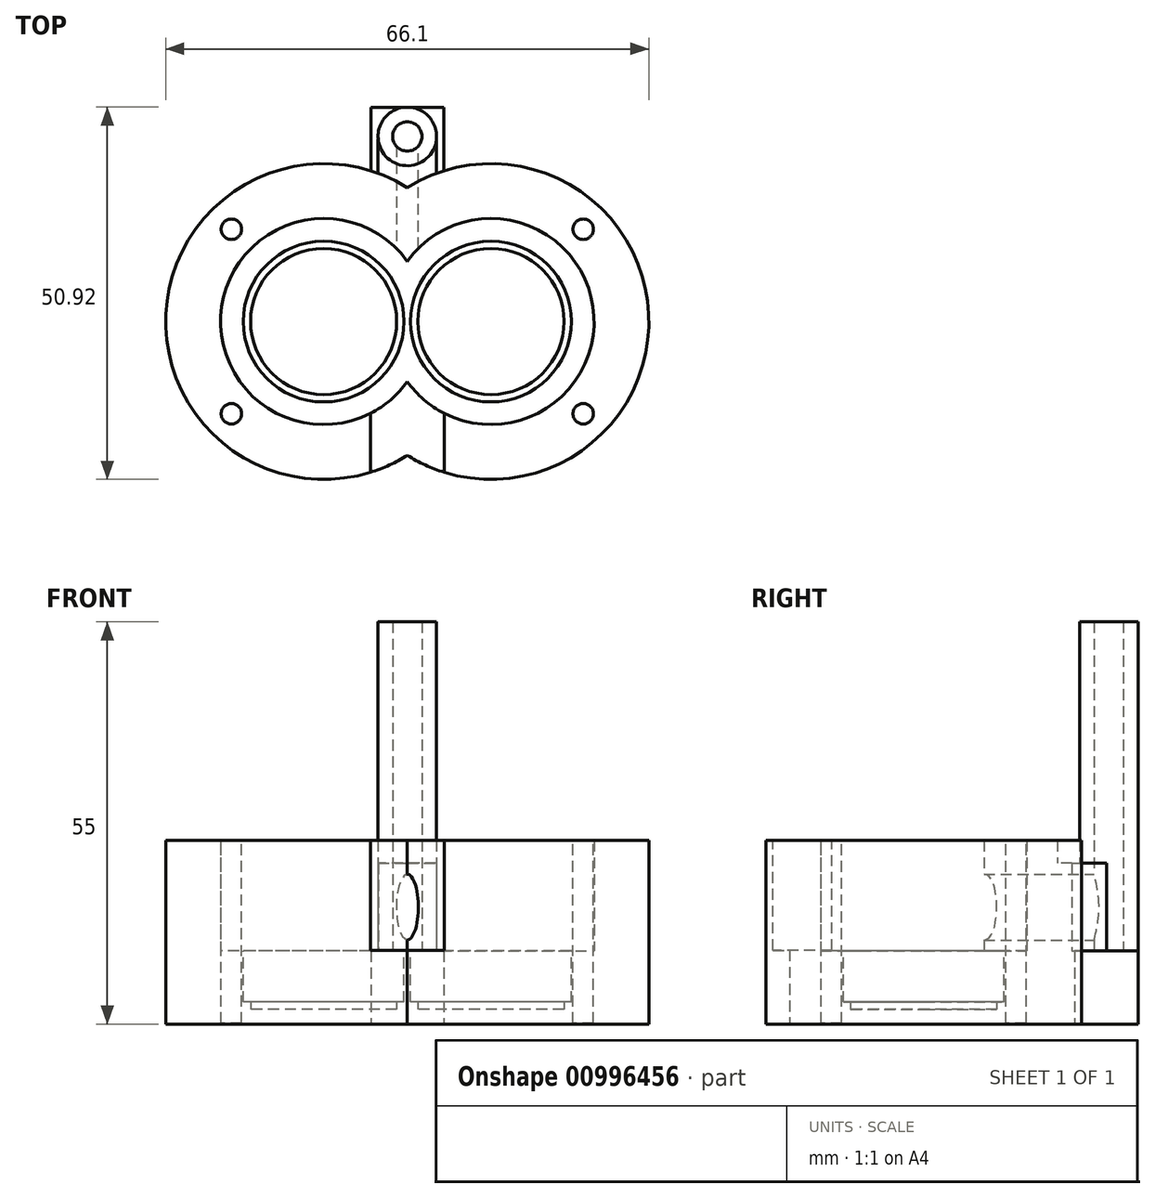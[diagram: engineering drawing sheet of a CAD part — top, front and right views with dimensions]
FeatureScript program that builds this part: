
annotation { "Feature Type Name" : "Feature", "Feature Type Description" : "" }
export const myFeature = defineFeature(function(context is Context, id is Id, definition is map)
    precondition{}
    {
        {
            var Q0;
            Q0=qCreatedBy(makeId("Top.planeOp"),FACE);
            var sketch = newSketch(context, id + "F0", { "sketchPlane" : qUnion([Q0])});
            skArc(sketch, "E0", {"start": v(0, 8.23) * mm, "mid": v(-25.55, 0) * mm, "end": v(0, -8.23) * mm});
            skLineSegment(sketch, "E1", {"start": v(-11.45, 0) * mm, "end": v(11.45, 0) * mm, "construction": true});
            skLineSegment(sketch, "E2", {"start": v(0, 0) * mm, "end": v(0, 8.23) * mm, "construction": true});
            skArc(sketch, "E3.0", {"start": v(0, 18.32) * mm, "mid": v(-33.05, 0) * mm, "end": v(0, -18.32) * mm});
            skLineSegment(sketch, "E4", {"start": v(0, -18.32) * mm, "end": v(0, 18.32) * mm, "construction": true});
            skArc(sketch, "E5.MirrorCS", {"start": v(0, 8.23) * mm, "mid": v(25.55, 0) * mm, "end": v(0, -8.23) * mm});
            skArc(sketch, "E6.MirrorCS", {"start": v(0, 18.32) * mm, "mid": v(33.05, 0) * mm, "end": v(0, -18.32) * mm});
            skSolve(sketch);
        }
        {
            var Q0;
            Q0=qSketchRegion(id+"F0",true);
            extrude(context, id + "F1", {"entities" : qUnion([Q0]), "depth" : 15.1 * mm, "offsetDistance" : 25 * mm});
        }
        {
            var Q0;
            Q0=makeQuery(id+"F1.opExtrude","CAP_FACE",FACE,{"disambiguationData":[OSD([sQuery(id+"F0.wireOp",EDGE,"E0"),sQuery(id+"F0.wireOp",EDGE,"E3.0"),sQuery(id+"F0.wireOp",EDGE,"E5.MirrorCS"),sQuery(id+"F0.wireOp",EDGE,"E6.MirrorCS")])],"isStart":true});
            var sketch = newSketch(context, id + "F2", { "sketchPlane" : qUnion([Q0])});
            skArc(sketch, "E7.0", {"start": v(0, -18.32) * mm, "mid": v(33.05, 0) * mm, "end": v(0, 18.32) * mm});
            skArc(sketch, "E8.0", {"start": v(0, -18.32) * mm, "mid": v(-33.05, 0) * mm, "end": v(0, 18.32) * mm});
            skSolve(sketch);
        }
        {
            var Q0;
            Q0=qSketchRegion(id+"F2",true);
            extrude(context, id + "F3", {"entities" : qUnion([Q0]), "operationType" : NewBodyOperationType.ADD, "depth" : 10 * mm, "offsetDistance" : 25 * mm});
        }
        {
            var Q0;
            Q0=makeQuery(id+"F3.opExtrude","CAP_FACE",FACE,{"disambiguationData":[OSD([sQuery(id+"F2.wireOp",EDGE,"E7.0"),sQuery(id+"F2.wireOp",EDGE,"E8.0")])],"isStart":true});
            var sketch = newSketch(context, id + "F4", { "sketchPlane" : qUnion([Q0])});
            skArc(sketch, "E9.0", {"start": v(0, 8.23) * mm, "mid": v(25.55, 0) * mm, "end": v(0, -8.23) * mm, "construction": true});
            skArc(sketch, "E10.0", {"start": v(0, 8.23) * mm, "mid": v(-25.55, 0) * mm, "end": v(0, -8.23) * mm, "construction": true});
            skCircle(sketch, "E11", {"center": v(-11.45, 0) * mm, "radius": 11 * mm});
            skCircle(sketch, "E12", {"center": v(11.45, 0) * mm, "radius": 11 * mm});
            skSolve(sketch);
        }
        {
            var Q0;
            Q0=qSketchRegion(id+"F4",true);
            extrude(context, id + "F5", {"entities" : qUnion([Q0]), "operationType" : NewBodyOperationType.REMOVE, "oppositeDirection" : true, "depth" : 8 * mm, "offsetDistance" : 25 * mm});
        }
        {
            var Q0;
            Q0=makeQuery(id+"F5.boolean.opBoolean","COPY",FACE,{"derivedFrom":makeQuery(id+"F5.opExtrude","CAP_FACE",FACE,{"disambiguationData":[OSD([sQuery(id+"F4.wireOp",EDGE,"E11")])],"isStart":false})});
            var sketch = newSketch(context, id + "F6", { "sketchPlane" : qUnion([Q0])});
            skCircle(sketch, "E13.0", {"center": v(-11.45, 0) * mm, "radius": 11 * mm});
            skCircle(sketch, "E14.0", {"center": v(11.45, 0) * mm, "radius": 11 * mm});
            skCircle(sketch, "E15.0", {"center": v(-11.45, 0) * mm, "radius": 10 * mm});
            skCircle(sketch, "E16.0", {"center": v(11.45, 0) * mm, "radius": 10 * mm});
            skSolve(sketch);
        }
        {
            var Q0;
            Q0=qSketchRegion(id+"F6",true);
            extrude(context, id + "F7", {"entities" : qUnion([Q0]), "operationType" : NewBodyOperationType.ADD, "depth" : 1 * mm, "offsetDistance" : 25 * mm});
        }
        {
            var Q0;
            Q0=makeQuery(id+"F1.opExtrude","CAP_FACE",FACE,{"disambiguationData":[OSD([sQuery(id+"F0.wireOp",EDGE,"E0"),sQuery(id+"F0.wireOp",EDGE,"E3.0"),sQuery(id+"F0.wireOp",EDGE,"E5.MirrorCS"),sQuery(id+"F0.wireOp",EDGE,"E6.MirrorCS")])],"isStart":false});
            var sketch = newSketch(context, id + "F8", { "sketchPlane" : qUnion([Q0])});
            skArc(sketch, "E17.0", {"start": v(-5.05, -12.56) * mm, "mid": v(-2.26, -10.7) * mm, "end": v(0, -8.23) * mm});
            skArc(sketch, "E18.0", {"start": v(-5.05, -20.63) * mm, "mid": v(-2.45, -19.64) * mm, "end": v(0, -18.32) * mm});
            skArc(sketch, "E19.0", {"start": v(5.05, -20.63) * mm, "mid": v(2.45, -19.64) * mm, "end": v(0, -18.32) * mm});
            skArc(sketch, "E20.0", {"start": v(5.05, -12.56) * mm, "mid": v(2.26, -10.7) * mm, "end": v(0, -8.23) * mm});
            skLineSegment(sketch, "E21", {"start": v(-5.05, -12.56) * mm, "end": v(-5.05, -20.63) * mm});
            skLineSegment(sketch, "E22", {"start": v(5.05, -12.56) * mm, "end": v(5.05, -20.63) * mm});
            skLineSegment(sketch, "E23", {"start": v(0, -8.23) * mm, "end": v(0, -18.32) * mm, "construction": true});
            skLineSegment(sketch, "E24", {"start": v(-5.05, -12.56) * mm, "end": v(0, -12.56) * mm, "construction": true});
            skLineSegment(sketch, "E25", {"start": v(0, -12.56) * mm, "end": v(5.05, -12.56) * mm, "construction": true});
            skPoint(sketch, "E26.orphan", {"position": v(0, 8.23) * mm});
            skPoint(sketch, "E27.orphan", {"position": v(0, 18.32) * mm});
            skSolve(sketch);
        }
        {
            var Q0;
            Q0=qSketchRegion(id+"F8",true);
            extrude(context, id + "F9", {"entities" : qUnion([Q0]), "operationType" : NewBodyOperationType.REMOVE, "oppositeDirection" : true, "depth" : 15 * mm, "offsetDistance" : 25 * mm});
        }
        {
            var Q0;
            Q0=makeQuery(id+"F3.opExtrude","CAP_FACE",FACE,{"disambiguationData":[OSD([sQuery(id+"F2.wireOp",EDGE,"E7.0"),sQuery(id+"F2.wireOp",EDGE,"E8.0")])],"isStart":false});
            var sketch = newSketch(context, id + "F10", { "sketchPlane" : qUnion([Q0])});
            skArc(sketch, "E28.0", {"start": v(0, -18.32) * mm, "mid": v(-32.87, -2.78) * mm, "end": v(-5.05, 20.63) * mm});
            skArc(sketch, "E29.0", {"start": v(0, -18.32) * mm, "mid": v(32.87, -2.78) * mm, "end": v(5.05, 20.63) * mm});
            skLineSegment(sketch, "E30", {"start": v(-5, -20.61) * mm, "end": v(-5, -29.32) * mm});
            skLineSegment(sketch, "E31", {"start": v(-5, -29.32) * mm, "end": v(0, -29.32) * mm});
            skLineSegment(sketch, "E32", {"start": v(5, -29.32) * mm, "end": v(5, -20.61) * mm});
            skLineSegment(sketch, "E33", {"start": v(0, -29.32) * mm, "end": v(5, -29.32) * mm});
            skLineSegment(sketch, "E34", {"start": v(0, -18.32) * mm, "end": v(0, -29.32) * mm, "construction": true});
            skSolve(sketch);
        }
        {
            var Q0;
            Q0=qSketchRegion(id+"F10",true);
            var Q1;
            Q1=makeQuery(id+"F1.opExtrude","CAP_FACE",FACE,{"disambiguationData":[OSD([sQuery(id+"F0.wireOp",EDGE,"E0"),sQuery(id+"F0.wireOp",EDGE,"E3.0"),sQuery(id+"F0.wireOp",EDGE,"E5.MirrorCS"),sQuery(id+"F0.wireOp",EDGE,"E6.MirrorCS")])],"isStart":false});
            extrude(context, id + "F11", {"entities" : qUnion([Q0]), "operationType" : NewBodyOperationType.ADD, "oppositeDirection" : true, "depth" : 10 * mm, "endBoundEntityFace" : qUnion([Q1]), "offsetDistance" : 25 * mm});
        }
        {
            var Q0;
            Q0=makeQuery(id+"F11.opExtrude","CAP_FACE",FACE,{"disambiguationData":[OSD([sQuery(id+"F10.wireOp",EDGE,"E28.0"),sQuery(id+"F10.wireOp",EDGE,"E29.0"),sQuery(id+"F10.wireOp",EDGE,"E30"),sQuery(id+"F10.wireOp",EDGE,"E31"),sQuery(id+"F10.wireOp",EDGE,"E32"),sQuery(id+"F10.wireOp",EDGE,"E33")])],"isStart":false});
            var sketch = newSketch(context, id + "F12", { "sketchPlane" : qUnion([Q0])});
            skCircle(sketch, "E35", {"center": v(0, 25.32) * mm, "radius": 2 * mm});
            skCircle(sketch, "E36.0", {"center": v(0, 25.32) * mm, "radius": 4 * mm});
            skSolve(sketch);
        }
        {
            var Q0;
            Q0=qSketchRegion(id+"F12",true);
            extrude(context, id + "F13", {"entities" : qUnion([Q0]), "operationType" : NewBodyOperationType.ADD, "depth" : 45 * mm, "offsetDistance" : 25 * mm});
        }
        {
            var Q0;
            Q0=qCreatedBy(makeId("Front.planeOp"),FACE);
            cPlane(context, id + "F14", {"entities" : qUnion([Q0]), "cplaneType" : CPlaneType.OFFSET, "offset" : 25 * mm, "oppositeDirection" : true, "width" : 150 * mm, "height" : 150 * mm});
        }
        {
            var Q0;
            Q0=qCreatedBy(id+"F14.planeOp",FACE);
            var sketch = newSketch(context, id + "F15", { "sketchPlane" : qUnion([Q0])});
            skLineSegment(sketch, "E37", {"start": v(4, 12) * mm, "end": v(4, 0) * mm});
            skLineSegment(sketch, "E38", {"start": v(-4, 0) * mm, "end": v(-4, 12) * mm});
            skLineSegment(sketch, "E39", {"start": v(4, 12) * mm, "end": v(-4, 12) * mm});
            skLineSegment(sketch, "E40", {"start": v(4, 0) * mm, "end": v(-4, 0) * mm});
            skSolve(sketch);
        }
        {
            var Q0;
            Q0=qSketchRegion(id+"F15",true);
            extrude(context, id + "F16", {"entities" : qUnion([Q0]), "operationType" : NewBodyOperationType.ADD, "depth" : 8 * mm, "offsetDistance" : 25 * mm});
        }
        {
            var Q0;
            {var subQ0=sQuery(id+"F15.wireOp",EDGE,"E39");Q0=makeQuery(id+"F16.boolean.opBoolean","SPLIT",FACE,{"disambiguationData":[TD([makeQuery(id+"F13.opExtrude","SWEPT_FACE",FACE,{"disambiguationData":[OSD([sQuery(id+"F12.wireOp",EDGE,"E35")])]})])],"derivedFrom":makeQuery(id+"F16.opExtrude","CAP_FACE",FACE,{"disambiguationData":[OSD([sQuery(id+"F15.wireOp",EDGE,"E37"),sQuery(id+"F15.wireOp",EDGE,"E38"),subQ0,sQuery(id+"F15.wireOp",EDGE,"E40")])],"isStart":true})});}
            var sketch = newSketch(context, id + "F17", { "sketchPlane" : qUnion([Q0])});
            skEllipse(sketch, "E41", {"center": v(0, 6) * mm, "majorRadius": 4.5 * mm, "minorRadius": 1.5 * mm, "majorAxis": v(0, -1)});
            skSolve(sketch);
        }
        {
            var Q0;
            Q0=qSketchRegion(id+"F17",true);
            extrude(context, id + "F18", {"entities" : qUnion([Q0]), "operationType" : NewBodyOperationType.REMOVE, "oppositeDirection" : true, "depth" : 25 * mm, "offsetDistance" : 25 * mm});
        }
        {
            var Q0;
            {var subQ0=sQuery(id+"F15.wireOp",EDGE,"E39");Q0=makeQuery(id+"F16.boolean.opBoolean","SPLIT",FACE,{"disambiguationData":[TD([makeQuery(id+"F13.opExtrude","SWEPT_FACE",FACE,{"disambiguationData":[OSD([sQuery(id+"F12.wireOp",EDGE,"E35")])]})])],"derivedFrom":makeQuery(id+"F16.opExtrude","SWEPT_FACE",FACE,{"disambiguationData":[OSD([subQ0])]})});}
            var sketch = newSketch(context, id + "F19", { "sketchPlane" : qUnion([Q0])});
            skArc(sketch, "E42.0.0", {"start": v(-1.97, 25) * mm, "mid": v(0, 23.32) * mm, "end": v(1.97, 25) * mm});
            skLineSegment(sketch, "E42.0.1", {"start": v(1.97, 25) * mm, "end": v(-1.97, 25) * mm});
            skSolve(sketch);
        }
        {
            var Q0;
            Q0=qSketchRegion(id+"F19",true);
            var Q1;
            Q1=makeQuery(id+"F13.boolean.opBoolean","SPLIT",FACE,{"disambiguationData":[TD([makeQuery(id+"F13.opExtrude","SWEPT_FACE",FACE,{"disambiguationData":[OSD([sQuery(id+"F12.wireOp",EDGE,"E35")])]})])],"derivedFrom":makeQuery(id+"F11.opExtrude","CAP_FACE",FACE,{"disambiguationData":[OSD([sQuery(id+"F10.wireOp",EDGE,"E28.0"),sQuery(id+"F10.wireOp",EDGE,"E29.0"),sQuery(id+"F10.wireOp",EDGE,"E30"),sQuery(id+"F10.wireOp",EDGE,"E31"),sQuery(id+"F10.wireOp",EDGE,"E32"),sQuery(id+"F10.wireOp",EDGE,"E33")])],"isStart":false})});
            extrude(context, id + "F20", {"entities" : qUnion([Q0]), "operationType" : NewBodyOperationType.REMOVE, "endBound" : BoundingType.UP_TO_SURFACE, "oppositeDirection" : true, "depth" : 25 * mm, "endBoundEntityFace" : qUnion([Q1]), "offsetDistance" : 25 * mm});
        }
        {
            var Q0;
            Q0=makeQuery(id+"F1.opExtrude","CAP_FACE",FACE,{"disambiguationData":[OSD([sQuery(id+"F0.wireOp",EDGE,"E0"),sQuery(id+"F0.wireOp",EDGE,"E3.0"),sQuery(id+"F0.wireOp",EDGE,"E5.MirrorCS"),sQuery(id+"F0.wireOp",EDGE,"E6.MirrorCS")])],"isStart":false});
            var sketch = newSketch(context, id + "F21", { "sketchPlane" : qUnion([Q0])});
            skArc(sketch, "E43.0", {"start": v(0, 8.23) * mm, "mid": v(-25.15, 3.33) * mm, "end": v(-5.05, -12.56) * mm, "construction": true});
            skLineSegment(sketch, "E44", {"start": v(-11.45, 0) * mm, "end": v(-21.42, 9.97) * mm, "construction": true});
            skLineSegment(sketch, "E45", {"start": v(-21.42, 9.97) * mm, "end": v(-24.07, 12.62) * mm, "construction": true});
            skLineSegment(sketch, "E46", {"start": v(-24.07, 12.62) * mm, "end": v(-26.72, 15.27) * mm, "construction": true});
            skCircle(sketch, "E47", {"center": v(-24.07, 12.62) * mm, "radius": 1.4 * mm});
            skLineSegment(sketch, "E48", {"start": v(-11.45, 0) * mm, "end": v(-25.55, 0) * mm, "construction": true});
            skLineSegment(sketch, "E49", {"start": v(0, 8.23) * mm, "end": v(0, 0) * mm, "construction": true});
            skCircle(sketch, "E50.MirrorC", {"center": v(-24.07, -12.62) * mm, "radius": 1.4 * mm});
            skCircle(sketch, "E51.MirrorC", {"center": v(24.07, 12.62) * mm, "radius": 1.4 * mm});
            skCircle(sketch, "E52.MirrorC", {"center": v(24.07, -12.62) * mm, "radius": 1.4 * mm});
            skSolve(sketch);
        }
        {
            var Q0;
            Q0=qSketchRegion(id+"F21",true);
            extrude(context, id + "F22", {"entities" : qUnion([Q0]), "operationType" : NewBodyOperationType.REMOVE, "oppositeDirection" : true, "depth" : 25 * mm, "offsetDistance" : 25 * mm});
        }
    });
